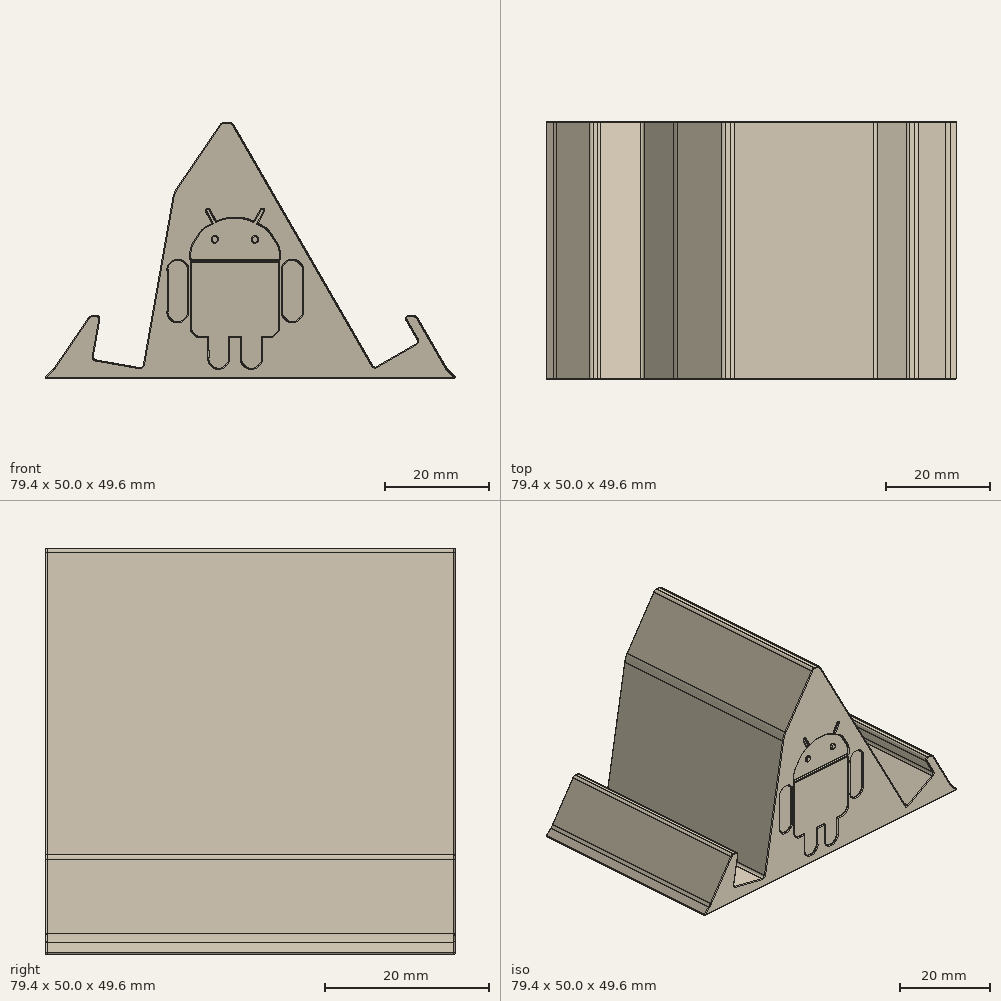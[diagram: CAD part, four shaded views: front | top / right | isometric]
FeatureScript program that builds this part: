
annotation { "Feature Type Name" : "Feature", "Feature Type Description" : "" }
export const myFeature = defineFeature(function(context is Context, id is Id, definition is map)
    precondition{}
    {
        {
            var Q0;
            Q0=qCreatedBy(makeId("Front.planeOp"),FACE);
            var sketch = newSketch(context, id + "F0", { "sketchPlane" : qUnion([Q0])});
            skLineSegment(sketch, "E0", {"start": v(-5.77, 0) * mm, "end": v(5.77, 0) * mm});
            skLineSegment(sketch, "E1", {"start": v(5.77, 0) * mm, "end": v(-0.11, 10.2) * mm});
            skLineSegment(sketch, "E2", {"start": v(0, 0) * mm, "end": v(0, -5.44) * mm, "construction": true});
            skLineSegment(sketch, "E3", {"start": v(-5.77, 0) * mm, "end": v(-33.27, 47.63) * mm});
            skLineSegment(sketch, "E4", {"start": v(-69.73, -2) * mm, "end": v(10.27, -2) * mm});
            skLineSegment(sketch, "E5", {"start": v(5.77, 0) * mm, "end": v(8.27, 0) * mm, "construction": true});
            skLineSegment(sketch, "E6", {"start": v(8.27, 0) * mm, "end": v(10.27, -2) * mm});
            skLineSegment(sketch, "E7", {"start": v(-5.77, 0) * mm, "end": v(-7.77, 0) * mm, "construction": true});
            skLineSegment(sketch, "E8", {"start": v(-69.73, -2) * mm, "end": v(-67.73, 0) * mm});
            skLineSegment(sketch, "E9", {"start": v(-7.77, 0) * mm, "end": v(-35.27, 47.63) * mm});
            skLineSegment(sketch, "E10", {"start": v(-35.27, 47.63) * mm, "end": v(-33.27, 47.63) * mm});
            skLineSegment(sketch, "E11", {"start": v(8.27, 0) * mm, "end": v(2.39, 10.2) * mm});
            skLineSegment(sketch, "E12", {"start": v(2.39, 10.2) * mm, "end": v(-0.11, 10.2) * mm});
            skLineSegment(sketch, "E13", {"start": v(-7.77, 0) * mm, "end": v(-67.73, 0) * mm});
            skLineSegment(sketch, "E14", {"start": v(8.27, 0) * mm, "end": v(8.27, 0) * mm});
            skLineSegment(sketch, "E15", {"start": v(-5.77, 0) * mm, "end": v(2.89, 5) * mm});
            skSolve(sketch);
        }
        {
            var Q0;
            Q0=makeQuery(id+"F0.imprint","IMPRINT",FACE,{"disambiguationData":[TD([[makeQuery(id+"F0.imprint","IMPRINT",EDGE,{"derivedFrom":sQuery(id+"F0.wireOp",EDGE,"E0")}),-1.0]])]});
            var Q1;
            {var subQ0=sQuery(id+"F0.wireOp",EDGE,"E0");Q1=makeQuery(id+"F0.imprint","IMPRINT",FACE,{"disambiguationData":[TD([[makeQuery(id+"F0.imprint","IMPRINT",EDGE,{"derivedFrom":subQ0}),1.0]])]});}
            extrude(context, id + "F1", {"entities" : qUnion([Q0, Q1]), "depth" : 50 * mm});
        }
        {
            var Q0;
            Q0=qCreatedBy(makeId("Top.planeOp"),FACE);
            var sketch = newSketch(context, id + "F2", { "sketchPlane" : qUnion([Q0])});
            skPoint(sketch, "E16.0", {"position": v(-69.73, -25) * mm});
            skPoint(sketch, "E16.1", {"position": v(-35.27, -25) * mm});
            skLineSegment(sketch, "E17.bottom", {"start": v(-69.73, -3) * mm, "end": v(-7.77, -3) * mm});
            skLineSegment(sketch, "E17.top", {"start": v(-69.73, -47) * mm, "end": v(-7.77, -47) * mm});
            skLineSegment(sketch, "E17.left", {"start": v(-69.73, -3) * mm, "end": v(-69.73, -47) * mm});
            skLineSegment(sketch, "E17.right", {"start": v(-7.77, -3) * mm, "end": v(-7.77, -47) * mm});
            skPoint(sketch, "E18.1", {"position": v(-7.77, -25) * mm});
            skPoint(sketch, "E19.0", {"position": v(-69.73, 0) * mm});
            skSolve(sketch);
        }
        {
            var Q0;
            Q0=makeQuery(id+"F2.imprint","IMPRINT",FACE,{"disambiguationData":[TD([[makeQuery(id+"F2.imprint","IMPRINT",EDGE,{"derivedFrom":sQuery(id+"F2.wireOp",EDGE,"E17.bottom")}),-1.0]])]});
            extrude(context, id + "F3", {"entities" : qUnion([Q0]), "operationType" : NewBodyOperationType.REMOVE, "endBound" : BoundingType.THROUGH_ALL, "oppositeDirection" : true, "depth" : 25 * mm});
        }
        {
            var Q0;
            Q0=makeQuery(id+"F1.opExtrude","CAP_FACE",FACE,{"disambiguationData":[OSD([sQuery(id+"F0.wireOp",EDGE,"E1"),sQuery(id+"F0.wireOp",EDGE,"E3"),sQuery(id+"F0.wireOp",EDGE,"E4"),sQuery(id+"F0.wireOp",EDGE,"E6"),sQuery(id+"F0.wireOp",EDGE,"E8"),sQuery(id+"F0.wireOp",EDGE,"E9"),sQuery(id+"F0.wireOp",EDGE,"E10"),sQuery(id+"F0.wireOp",EDGE,"E11"),sQuery(id+"F0.wireOp",EDGE,"E12"),sQuery(id+"F0.wireOp",EDGE,"E13"),sQuery(id+"F0.wireOp",EDGE,"E14"),sQuery(id+"F0.wireOp",EDGE,"E15")])],"isStart":false});
            var sketch = newSketch(context, id + "F4", { "sketchPlane" : qUnion([Q0])});
            skPoint(sketch, "E20.0", {"position": v(-67.73, 0) * mm});
            skPoint(sketch, "E21.0", {"position": v(-35.27, 47.63) * mm});
            skLineSegment(sketch, "E22", {"start": v(-67.73, 0) * mm, "end": v(-35.27, 47.63) * mm});
            skLineSegment(sketch, "E23", {"start": v(-65.55, 0) * mm, "end": v(-34.27, 45.9) * mm});
            skLineSegment(sketch, "E24", {"start": v(-35.27, 47.63) * mm, "end": v(-34.27, 45.9) * mm});
            skLineSegment(sketch, "E25", {"start": v(-67.73, 0) * mm, "end": v(-65.55, 0) * mm});
            skSolve(sketch);
        }
        {
            var Q0;
            Q0=makeQuery(id+"F4.imprint","IMPRINT",FACE,{"disambiguationData":[TD([[makeQuery(id+"F4.imprint","IMPRINT",EDGE,{"derivedFrom":sQuery(id+"F4.wireOp",EDGE,"E22")}),-1.0]])]});
            var Q1;
            Q1=makeQuery(id+"F3.boolean.opBoolean","COPY",FACE,{"derivedFrom":makeQuery(id+"F3.opExtrude","SWEPT_FACE",FACE,{"disambiguationData":[OSD([sQuery(id+"F2.wireOp",EDGE,"E17.top")])]})});
            extrude(context, id + "F5", {"entities" : qUnion([Q0]), "operationType" : NewBodyOperationType.ADD, "endBound" : BoundingType.UP_TO_SURFACE, "oppositeDirection" : true, "endBoundEntityFace" : qUnion([Q1]), "depth" : 25 * mm});
        }
        {
            var Q0;
            Q0=makeQuery(id+"F1.opExtrude","CAP_FACE",FACE,{"disambiguationData":[OSD([sQuery(id+"F0.wireOp",EDGE,"E1"),sQuery(id+"F0.wireOp",EDGE,"E3"),sQuery(id+"F0.wireOp",EDGE,"E4"),sQuery(id+"F0.wireOp",EDGE,"E6"),sQuery(id+"F0.wireOp",EDGE,"E8"),sQuery(id+"F0.wireOp",EDGE,"E9"),sQuery(id+"F0.wireOp",EDGE,"E10"),sQuery(id+"F0.wireOp",EDGE,"E11"),sQuery(id+"F0.wireOp",EDGE,"E12"),sQuery(id+"F0.wireOp",EDGE,"E13"),sQuery(id+"F0.wireOp",EDGE,"E14"),sQuery(id+"F0.wireOp",EDGE,"E15")])],"isStart":true});
            var sketch = newSketch(context, id + "F6", { "sketchPlane" : qUnion([Q0])});
            skPoint(sketch, "E26.0", {"position": v(35.27, 47.63) * mm});
            skPoint(sketch, "E26.1", {"position": v(67.73, 0) * mm});
            skLineSegment(sketch, "E27", {"start": v(67.73, 0) * mm, "end": v(35.27, 47.63) * mm});
            skLineSegment(sketch, "E28", {"start": v(65.55, 0) * mm, "end": v(34.27, 45.9) * mm});
            skLineSegment(sketch, "E29", {"start": v(34.27, 45.9) * mm, "end": v(35.27, 47.63) * mm});
            skLineSegment(sketch, "E30", {"start": v(65.55, 0) * mm, "end": v(67.73, 0) * mm});
            skSolve(sketch);
        }
        {
            var Q0;
            Q0=makeQuery(id+"F6.imprint","IMPRINT",FACE,{"disambiguationData":[TD([[makeQuery(id+"F6.imprint","IMPRINT",EDGE,{"derivedFrom":sQuery(id+"F6.wireOp",EDGE,"E27")}),1.0]])]});
            var Q1;
            Q1=makeQuery(id+"F3.boolean.opBoolean","COPY",FACE,{"derivedFrom":makeQuery(id+"F3.opExtrude","SWEPT_FACE",FACE,{"disambiguationData":[OSD([sQuery(id+"F2.wireOp",EDGE,"E17.bottom")])]})});
            extrude(context, id + "F7", {"entities" : qUnion([Q0]), "operationType" : NewBodyOperationType.ADD, "endBound" : BoundingType.UP_TO_SURFACE, "oppositeDirection" : true, "endBoundEntityFace" : qUnion([Q1]), "depth" : 25 * mm});
        }
        {
            var Q0;
            {var subQ2=sQuery(id+"F0.wireOp",EDGE,"E13");Q0=makeQuery(id+"F3.boolean.opBoolean","SPLIT",FACE,{"disambiguationData":[TD([makeQuery(id+"F3.opExtrude","SWEPT_FACE",FACE,{"disambiguationData":[OSD([sQuery(id+"F2.wireOp",EDGE,"E17.top")])]})])],"derivedFrom":makeQuery(id+"F1.opExtrude","SWEPT_FACE",FACE,{"disambiguationData":[OSD([subQ2])]})});}
            var Q1;
            {var subQ2=sQuery(id+"F0.wireOp",EDGE,"E13");Q1=makeQuery(id+"F3.boolean.opBoolean","SPLIT",FACE,{"disambiguationData":[TD([makeQuery(id+"F3.opExtrude","SWEPT_FACE",FACE,{"disambiguationData":[OSD([sQuery(id+"F2.wireOp",EDGE,"E17.bottom")])]})])],"derivedFrom":makeQuery(id+"F1.opExtrude","SWEPT_FACE",FACE,{"disambiguationData":[OSD([subQ2])]})});}
            var Q2;
            Q2=makeQuery(id+"F1.opExtrude","SWEPT_BODY",BODY,{"disambiguationData":[OSD([sQuery(id+"F0.wireOp",EDGE,"E1"),sQuery(id+"F0.wireOp",EDGE,"E3"),sQuery(id+"F0.wireOp",EDGE,"E4"),sQuery(id+"F0.wireOp",EDGE,"E6"),sQuery(id+"F0.wireOp",EDGE,"E8"),sQuery(id+"F0.wireOp",EDGE,"E9"),sQuery(id+"F0.wireOp",EDGE,"E10"),sQuery(id+"F0.wireOp",EDGE,"E11"),sQuery(id+"F0.wireOp",EDGE,"E12"),sQuery(id+"F0.wireOp",EDGE,"E13"),sQuery(id+"F0.wireOp",EDGE,"E14"),sQuery(id+"F0.wireOp",EDGE,"E15")])]});
            extrude(context, id + "F8", {"entities" : qUnion([Q0, Q1]), "operationType" : NewBodyOperationType.ADD, "endBound" : BoundingType.UP_TO_BODY, "endBoundEntityBody" : qUnion([Q2]), "depth" : 25 * mm});
        }
        {
            var Q0;
            {var subQ0=sQuery(id+"F0.wireOp",EDGE,"E13");Q0=makeQuery(id+"F8.boolean.opBoolean","MERGE",FACE,{"derivedFrom":[makeQuery(id+"F5.boolean.opBoolean","MERGE",FACE,{"derivedFrom":[makeQuery(id+"F1.opExtrude","CAP_FACE",FACE,{"disambiguationData":[OSD([sQuery(id+"F0.wireOp",EDGE,"E1"),sQuery(id+"F0.wireOp",EDGE,"E3"),sQuery(id+"F0.wireOp",EDGE,"E4"),sQuery(id+"F0.wireOp",EDGE,"E6"),sQuery(id+"F0.wireOp",EDGE,"E8"),sQuery(id+"F0.wireOp",EDGE,"E9"),sQuery(id+"F0.wireOp",EDGE,"E10"),sQuery(id+"F0.wireOp",EDGE,"E11"),sQuery(id+"F0.wireOp",EDGE,"E12"),subQ0,sQuery(id+"F0.wireOp",EDGE,"E15")])],"isStart":false}),makeQuery(id+"F5.opExtrude","CAP_FACE",FACE,{"disambiguationData":[OSD([sQuery(id+"F4.wireOp",EDGE,"E22"),sQuery(id+"F4.wireOp",EDGE,"E23"),sQuery(id+"F4.wireOp",EDGE,"E24"),sQuery(id+"F4.wireOp",EDGE,"E25")])],"isStart":true})]}),makeQuery(id+"F8.opExtrude","SWEPT_FACE",FACE,{"disambiguationData":[OSD([subQ0]),TDD([makeQuery(id+"F1.opExtrude","CAP_EDGE",EDGE,{"disambiguationData":[OSD([subQ0])],"isStart":false})])]})]});}
            var sketch = newSketch(context, id + "F9", { "sketchPlane" : qUnion([Q0])});
            skLineSegment(sketch, "E31", {"start": v(-71.82, 0) * mm, "end": v(0, 0) * mm, "construction": true});
            skLineSegment(sketch, "E32", {"start": v(-60.58, 0) * mm, "end": v(-60.28, 1.71) * mm, "construction": true});
            skLineSegment(sketch, "E33", {"start": v(-53.78, 38.57) * mm, "end": v(-43.78, 38.57) * mm});
            skLineSegment(sketch, "E34", {"start": v(-43.78, 38.57) * mm, "end": v(-50.58, 0) * mm});
            skLineSegment(sketch, "E35", {"start": v(-50.58, 0) * mm, "end": v(-60.58, 0) * mm, "construction": true});
            skLineSegment(sketch, "E36", {"start": v(-50.58, 0) * mm, "end": v(-60.28, 1.71) * mm});
            skLineSegment(sketch, "E37", {"start": v(-60.28, 1.71) * mm, "end": v(-53.78, 38.57) * mm});
            skLineSegment(sketch, "E38", {"start": v(-58.78, 10.2) * mm, "end": v(-60.78, 10.2) * mm});
            skLineSegment(sketch, "E39", {"start": v(-50.58, 0) * mm, "end": v(-50.58, -2) * mm});
            skPoint(sketch, "E40.0", {"position": v(-35.27, 47.63) * mm});
            skLineSegment(sketch, "E41", {"start": v(-35.27, 47.63) * mm, "end": v(-33.62, 46.5) * mm});
            skLineSegment(sketch, "E42", {"start": v(-33.62, 46.5) * mm, "end": v(-42.74, 33.13) * mm});
            skLineSegment(sketch, "E43", {"start": v(-42.74, 33.13) * mm, "end": v(-48.58, 0) * mm});
            skLineSegment(sketch, "E44", {"start": v(-48.58, 0) * mm, "end": v(-48.58, -2) * mm});
            skLineSegment(sketch, "E45", {"start": v(-48.58, -2) * mm, "end": v(-50.58, -2) * mm});
            skLineSegment(sketch, "E46", {"start": v(-42.74, 33.13) * mm, "end": v(-44.74, 33.13) * mm, "construction": true});
            skSolve(sketch);
        }
        {
            var Q0;
            {var subQ0=sQuery(id+"F9.wireOp",EDGE,"E33");Q0=makeQuery(id+"F9.imprint","IMPRINT",FACE,{"disambiguationData":[TD([[makeQuery(id+"F9.imprint","IMPRINT",EDGE,{"derivedFrom":subQ0}),-1.0]])]});}
            var Q1;
            {var subQ4=sQuery(id+"F9.wireOp",EDGE,"E36");Q1=makeQuery(id+"F9.imprint","IMPRINT",FACE,{"disambiguationData":[TD([[makeQuery(id+"F9.imprint","IMPRINT",EDGE,{"derivedFrom":subQ4}),-1.0]])]});}
            var Q2;
            {var subQ0=sQuery(id+"F9.wireOp",EDGE,"E38");Q2=makeQuery(id+"F9.imprint","IMPRINT",FACE,{"disambiguationData":[TD([[makeQuery(id+"F9.imprint","IMPRINT",EDGE,{"derivedFrom":subQ0}),-1.0]])]});}
            extrude(context, id + "F10", {"entities" : qUnion([Q0, Q1, Q2]), "operationType" : NewBodyOperationType.REMOVE, "endBound" : BoundingType.THROUGH_ALL, "oppositeDirection" : true, "depth" : 25 * mm});
        }
        {
            var Q0;
            {var subQ2=sQuery(id+"F9.wireOp",EDGE,"E36");Q0=makeQuery(id+"F9.imprint","IMPRINT",FACE,{"disambiguationData":[TD([[makeQuery(id+"F9.imprint","IMPRINT",EDGE,{"derivedFrom":subQ2}),1.0]])]});}
            var Q1;
            {var subQ0=sQuery(id+"F2.wireOp",EDGE,"E17.bottom");Q1=makeQuery(id+"F8.boolean.opBoolean","MERGE",FACE,{"derivedFrom":[makeQuery(id+"F7.boolean.opBoolean","MERGE",FACE,{"derivedFrom":[makeQuery(id+"F3.boolean.opBoolean","COPY",FACE,{"derivedFrom":makeQuery(id+"F3.opExtrude","SWEPT_FACE",FACE,{"disambiguationData":[OSD([subQ0])]})}),makeQuery(id+"F7.opExtrude","CAP_FACE",FACE,{"disambiguationData":[OSD([sQuery(id+"F6.wireOp",EDGE,"E27"),sQuery(id+"F6.wireOp",EDGE,"E28"),sQuery(id+"F6.wireOp",EDGE,"E29"),sQuery(id+"F6.wireOp",EDGE,"E30")])],"isStart":false})]}),makeQuery(id+"F8.opExtrude","SWEPT_FACE",FACE,{"disambiguationData":[OSD([subQ0])]})]});}
            extrude(context, id + "F11", {"entities" : qUnion([Q0]), "operationType" : NewBodyOperationType.ADD, "endBound" : BoundingType.UP_TO_SURFACE, "oppositeDirection" : true, "endBoundEntityFace" : qUnion([Q1]), "depth" : 25 * mm});
        }
        {
            var Q0;
            {var subQ1=sQuery(id+"F9.wireOp",EDGE,"E39");Q0=makeQuery(id+"F9.imprint","IMPRINT",FACE,{"disambiguationData":[TD([[makeQuery(id+"F9.imprint","IMPRINT",EDGE,{"derivedFrom":subQ1}),1.0]])]});}
            var Q1;
            {var subQ0=sQuery(id+"F2.wireOp",EDGE,"E17.bottom");Q1=makeQuery(id+"F8.boolean.opBoolean","MERGE",FACE,{"derivedFrom":[makeQuery(id+"F7.boolean.opBoolean","MERGE",FACE,{"derivedFrom":[makeQuery(id+"F3.boolean.opBoolean","COPY",FACE,{"derivedFrom":makeQuery(id+"F3.opExtrude","SWEPT_FACE",FACE,{"disambiguationData":[OSD([subQ0])]})}),makeQuery(id+"F7.opExtrude","CAP_FACE",FACE,{"disambiguationData":[OSD([sQuery(id+"F6.wireOp",EDGE,"E27"),sQuery(id+"F6.wireOp",EDGE,"E28"),sQuery(id+"F6.wireOp",EDGE,"E29"),sQuery(id+"F6.wireOp",EDGE,"E30")])],"isStart":false})]}),makeQuery(id+"F8.opExtrude","SWEPT_FACE",FACE,{"disambiguationData":[OSD([subQ0])]})]});}
            extrude(context, id + "F12", {"entities" : qUnion([Q0]), "operationType" : NewBodyOperationType.ADD, "endBound" : BoundingType.UP_TO_SURFACE, "oppositeDirection" : true, "endBoundEntityFace" : qUnion([Q1]), "depth" : 25 * mm});
        }
        {
            var Q0;
            {var subQ0=sQuery(id+"F0.wireOp",EDGE,"E13");Q0=makeQuery(id+"F8.boolean.opBoolean","MERGE",FACE,{"derivedFrom":[makeQuery(id+"F5.boolean.opBoolean","MERGE",FACE,{"derivedFrom":[makeQuery(id+"F1.opExtrude","CAP_FACE",FACE,{"disambiguationData":[OSD([sQuery(id+"F0.wireOp",EDGE,"E1"),sQuery(id+"F0.wireOp",EDGE,"E3"),sQuery(id+"F0.wireOp",EDGE,"E4"),sQuery(id+"F0.wireOp",EDGE,"E6"),sQuery(id+"F0.wireOp",EDGE,"E8"),sQuery(id+"F0.wireOp",EDGE,"E9"),sQuery(id+"F0.wireOp",EDGE,"E10"),sQuery(id+"F0.wireOp",EDGE,"E11"),sQuery(id+"F0.wireOp",EDGE,"E12"),subQ0,sQuery(id+"F0.wireOp",EDGE,"E15")])],"isStart":false}),makeQuery(id+"F5.opExtrude","CAP_FACE",FACE,{"disambiguationData":[OSD([sQuery(id+"F4.wireOp",EDGE,"E22"),sQuery(id+"F4.wireOp",EDGE,"E23"),sQuery(id+"F4.wireOp",EDGE,"E24"),sQuery(id+"F4.wireOp",EDGE,"E25")])],"isStart":true})]}),makeQuery(id+"F8.opExtrude","SWEPT_FACE",FACE,{"disambiguationData":[OSD([subQ0]),TDD([makeQuery(id+"F1.opExtrude","CAP_EDGE",EDGE,{"disambiguationData":[OSD([subQ0])],"isStart":false})])]})]});}
            var sketch = newSketch(context, id + "F13", { "sketchPlane" : qUnion([Q0])});
            skFitSpline(sketch, "E47", {"points": [v(-43.8, 20.82) * mm, v(-44.33, 20.82) * mm, v(-44.78, 20.64) * mm, v(-45.15, 20.27) * mm]});
            skFitSpline(sketch, "E48", {"points": [v(-45.15, 20.27) * mm, v(-45.52, 19.9) * mm, v(-45.7, 19.45) * mm, v(-45.7, 18.94) * mm]});
            skLineSegment(sketch, "E49", {"start": v(-45.7, 18.94) * mm, "end": v(-45.7, 11) * mm});
            skFitSpline(sketch, "E50", {"points": [v(-45.7, 11) * mm, v(-45.7, 10.47) * mm, v(-45.52, 10.02) * mm, v(-45.15, 9.65) * mm]});
            skFitSpline(sketch, "E51", {"points": [v(-45.15, 9.65) * mm, v(-44.78, 9.28) * mm, v(-44.33, 9.1) * mm, v(-43.8, 9.1) * mm]});
            skFitSpline(sketch, "E52", {"points": [v(-43.8, 9.1) * mm, v(-43.27, 9.1) * mm, v(-42.82, 9.28) * mm, v(-42.46, 9.65) * mm]});
            skFitSpline(sketch, "E53", {"points": [v(-42.46, 9.65) * mm, v(-42.1, 10.02) * mm, v(-41.91, 10.47) * mm, v(-41.91, 11) * mm]});
            skLineSegment(sketch, "E54", {"start": v(-41.91, 11) * mm, "end": v(-41.91, 18.94) * mm});
            skFitSpline(sketch, "E55", {"points": [v(-41.91, 18.94) * mm, v(-41.91, 19.45) * mm, v(-42.1, 19.9) * mm, v(-42.47, 20.27) * mm]});
            skFitSpline(sketch, "E56", {"points": [v(-42.47, 20.27) * mm, v(-42.84, 20.64) * mm, v(-43.28, 20.82) * mm, v(-43.8, 20.82) * mm]});
            skLineSegment(sketch, "E57", {"start": v(-28.5, 27.95) * mm, "end": v(-27.2, 30.37) * mm});
            skFitSpline(sketch, "E58", {"points": [v(-27.2, 30.37) * mm, v(-27.11, 30.53) * mm, v(-27.14, 30.65) * mm, v(-27.29, 30.74) * mm]});
            skFitSpline(sketch, "E59", {"points": [v(-27.29, 30.74) * mm, v(-27.45, 30.81) * mm, v(-27.57, 30.77) * mm, v(-27.66, 30.63) * mm]});
            skLineSegment(sketch, "E60", {"start": v(-27.66, 30.63) * mm, "end": v(-28.99, 28.19) * mm});
            skFitSpline(sketch, "E61", {"points": [v(-28.99, 28.19) * mm, v(-30.16, 28.7) * mm, v(-31.4, 28.96) * mm, v(-32.7, 28.96) * mm]});
            skFitSpline(sketch, "E62", {"points": [v(-32.7, 28.96) * mm, v(-34, 28.96) * mm, v(-35.24, 28.7) * mm, v(-36.41, 28.19) * mm]});
            skLineSegment(sketch, "E63", {"start": v(-36.41, 28.19) * mm, "end": v(-37.74, 30.63) * mm});
            skFitSpline(sketch, "E64", {"points": [v(-37.74, 30.63) * mm, v(-37.83, 30.77) * mm, v(-37.95, 30.81) * mm, v(-38.11, 30.74) * mm]});
            skFitSpline(sketch, "E65", {"points": [v(-38.11, 30.74) * mm, v(-38.26, 30.65) * mm, v(-38.29, 30.53) * mm, v(-38.2, 30.37) * mm]});
            skLineSegment(sketch, "E66", {"start": v(-38.2, 30.37) * mm, "end": v(-36.9, 27.95) * mm});
            skFitSpline(sketch, "E67", {"points": [v(-36.9, 27.95) * mm, v(-38.22, 27.27) * mm, v(-39.28, 26.33) * mm, v(-40.07, 25.11) * mm]});
            skFitSpline(sketch, "E68", {"points": [v(-40.07, 25.11) * mm, v(-40.86, 23.9) * mm, v(-41.25, 22.57) * mm, v(-41.25, 21.13) * mm]});
            skLineSegment(sketch, "E69", {"start": v(-41.25, 21.13) * mm, "end": v(-24.17, 21.13) * mm});
            skFitSpline(sketch, "E70", {"points": [v(-24.17, 21.13) * mm, v(-24.17, 22.57) * mm, v(-24.56, 23.9) * mm, v(-25.35, 25.11) * mm]});
            skFitSpline(sketch, "E71", {"points": [v(-25.35, 25.11) * mm, v(-26.14, 26.33) * mm, v(-27.2, 27.27) * mm, v(-28.5, 27.95) * mm]});
            skFitSpline(sketch, "E72", {"points": [v(-36.09, 24.43) * mm, v(-36.23, 24.29) * mm, v(-36.4, 24.22) * mm, v(-36.6, 24.22) * mm]});
            skFitSpline(sketch, "E73", {"points": [v(-36.6, 24.22) * mm, v(-36.8, 24.22) * mm, v(-36.96, 24.29) * mm, v(-37.1, 24.43) * mm]});
            skFitSpline(sketch, "E74", {"points": [v(-37.1, 24.43) * mm, v(-37.23, 24.57) * mm, v(-37.3, 24.74) * mm, v(-37.3, 24.94) * mm]});
            skFitSpline(sketch, "E75", {"points": [v(-37.3, 24.94) * mm, v(-37.3, 25.14) * mm, v(-37.23, 25.3) * mm, v(-37.1, 25.45) * mm]});
            skFitSpline(sketch, "E76", {"points": [v(-37.1, 25.45) * mm, v(-36.96, 25.59) * mm, v(-36.8, 25.66) * mm, v(-36.6, 25.66) * mm]});
            skFitSpline(sketch, "E77", {"points": [v(-36.6, 25.66) * mm, v(-36.4, 25.66) * mm, v(-36.23, 25.59) * mm, v(-36.09, 25.45) * mm]});
            skFitSpline(sketch, "E78", {"points": [v(-36.09, 25.45) * mm, v(-35.95, 25.3) * mm, v(-35.88, 25.14) * mm, v(-35.88, 24.94) * mm]});
            skFitSpline(sketch, "E79", {"points": [v(-35.88, 24.94) * mm, v(-35.88, 24.74) * mm, v(-35.95, 24.57) * mm, v(-36.09, 24.43) * mm]});
            skFitSpline(sketch, "E80", {"points": [v(-28.3, 24.43) * mm, v(-28.44, 24.29) * mm, v(-28.6, 24.22) * mm, v(-28.8, 24.22) * mm]});
            skFitSpline(sketch, "E81", {"points": [v(-28.8, 24.22) * mm, v(-29, 24.22) * mm, v(-29.17, 24.29) * mm, v(-29.31, 24.43) * mm]});
            skFitSpline(sketch, "E82", {"points": [v(-29.31, 24.43) * mm, v(-29.45, 24.57) * mm, v(-29.52, 24.74) * mm, v(-29.52, 24.94) * mm]});
            skFitSpline(sketch, "E83", {"points": [v(-29.52, 24.94) * mm, v(-29.52, 25.14) * mm, v(-29.45, 25.3) * mm, v(-29.31, 25.45) * mm]});
            skFitSpline(sketch, "E84", {"points": [v(-29.31, 25.45) * mm, v(-29.17, 25.59) * mm, v(-29, 25.66) * mm, v(-28.8, 25.66) * mm]});
            skFitSpline(sketch, "E85", {"points": [v(-28.8, 25.66) * mm, v(-28.6, 25.66) * mm, v(-28.44, 25.59) * mm, v(-28.3, 25.45) * mm]});
            skFitSpline(sketch, "E86", {"points": [v(-28.3, 25.45) * mm, v(-28.17, 25.3) * mm, v(-28.1, 25.14) * mm, v(-28.1, 24.94) * mm]});
            skFitSpline(sketch, "E87", {"points": [v(-28.1, 24.94) * mm, v(-28.1, 24.74) * mm, v(-28.17, 24.57) * mm, v(-28.3, 24.43) * mm]});
            skFitSpline(sketch, "E88", {"points": [v(-41.18, 8.17) * mm, v(-41.18, 7.6) * mm, v(-40.98, 7.12) * mm, v(-40.59, 6.73) * mm]});
            skFitSpline(sketch, "E89", {"points": [v(-40.59, 6.73) * mm, v(-40.2, 6.34) * mm, v(-39.71, 6.14) * mm, v(-39.14, 6.14) * mm]});
            skLineSegment(sketch, "E90", {"start": v(-39.14, 6.14) * mm, "end": v(-37.78, 6.14) * mm});
            skLineSegment(sketch, "E91", {"start": v(-37.78, 6.14) * mm, "end": v(-37.76, 1.95) * mm});
            skFitSpline(sketch, "E92", {"points": [v(-37.76, 1.95) * mm, v(-37.76, 1.42) * mm, v(-37.58, 0.97) * mm, v(-37.2, 0.6) * mm]});
            skFitSpline(sketch, "E93", {"points": [v(-37.2, 0.6) * mm, v(-36.84, 0.23) * mm, v(-36.4, 0.05) * mm, v(-35.88, 0.05) * mm]});
            skFitSpline(sketch, "E94", {"points": [v(-35.88, 0.05) * mm, v(-35.35, 0.05) * mm, v(-34.9, 0.23) * mm, v(-34.53, 0.6) * mm]});
            skFitSpline(sketch, "E95", {"points": [v(-34.53, 0.6) * mm, v(-34.16, 0.97) * mm, v(-33.97, 1.42) * mm, v(-33.97, 1.95) * mm]});
            skLineSegment(sketch, "E96", {"start": v(-33.97, 1.95) * mm, "end": v(-33.97, 6.14) * mm});
            skLineSegment(sketch, "E97", {"start": v(-33.97, 6.14) * mm, "end": v(-31.43, 6.14) * mm});
            skLineSegment(sketch, "E98", {"start": v(-31.43, 6.14) * mm, "end": v(-31.43, 1.95) * mm});
            skFitSpline(sketch, "E99", {"points": [v(-31.43, 1.95) * mm, v(-31.43, 1.42) * mm, v(-31.24, 0.97) * mm, v(-30.87, 0.6) * mm]});
            skFitSpline(sketch, "E100", {"points": [v(-30.87, 0.6) * mm, v(-30.5, 0.23) * mm, v(-30.05, 0.05) * mm, v(-29.52, 0.05) * mm]});
            skFitSpline(sketch, "E101", {"points": [v(-29.52, 0.05) * mm, v(-29, 0.05) * mm, v(-28.55, 0.23) * mm, v(-28.18, 0.6) * mm]});
            skFitSpline(sketch, "E102", {"points": [v(-28.18, 0.6) * mm, v(-27.8, 0.97) * mm, v(-27.62, 1.42) * mm, v(-27.62, 1.95) * mm]});
            skLineSegment(sketch, "E103", {"start": v(-27.62, 1.95) * mm, "end": v(-27.62, 6.14) * mm});
            skLineSegment(sketch, "E104", {"start": v(-27.62, 6.14) * mm, "end": v(-26.24, 6.14) * mm});
            skFitSpline(sketch, "E105", {"points": [v(-26.24, 6.14) * mm, v(-25.68, 6.14) * mm, v(-25.21, 6.34) * mm, v(-24.82, 6.73) * mm]});
            skFitSpline(sketch, "E106", {"points": [v(-24.82, 6.73) * mm, v(-24.42, 7.12) * mm, v(-24.23, 7.6) * mm, v(-24.23, 8.17) * mm]});
            skLineSegment(sketch, "E107", {"start": v(-24.23, 8.17) * mm, "end": v(-24.23, 20.47) * mm});
            skLineSegment(sketch, "E108", {"start": v(-24.23, 20.47) * mm, "end": v(-41.18, 20.47) * mm});
            skLineSegment(sketch, "E109", {"start": v(-41.18, 20.47) * mm, "end": v(-41.18, 8.17) * mm});
            skFitSpline(sketch, "E110", {"points": [v(-21.6, 20.82) * mm, v(-22.12, 20.82) * mm, v(-22.56, 20.64) * mm, v(-22.93, 20.28) * mm]});
            skFitSpline(sketch, "E111", {"points": [v(-22.93, 20.28) * mm, v(-23.3, 19.91) * mm, v(-23.49, 19.47) * mm, v(-23.49, 18.94) * mm]});
            skLineSegment(sketch, "E112", {"start": v(-23.49, 18.94) * mm, "end": v(-23.49, 11) * mm});
            skFitSpline(sketch, "E113", {"points": [v(-23.49, 11) * mm, v(-23.49, 10.47) * mm, v(-23.3, 10.02) * mm, v(-22.93, 9.65) * mm]});
            skFitSpline(sketch, "E114", {"points": [v(-22.93, 9.65) * mm, v(-22.56, 9.28) * mm, v(-22.12, 9.1) * mm, v(-21.6, 9.1) * mm]});
            skFitSpline(sketch, "E115", {"points": [v(-21.6, 9.1) * mm, v(-21.07, 9.1) * mm, v(-20.62, 9.28) * mm, v(-20.25, 9.65) * mm]});
            skFitSpline(sketch, "E116", {"points": [v(-20.25, 9.65) * mm, v(-19.88, 10.02) * mm, v(-19.7, 10.47) * mm, v(-19.7, 11) * mm]});
            skLineSegment(sketch, "E117", {"start": v(-19.7, 11) * mm, "end": v(-19.7, 18.94) * mm});
            skFitSpline(sketch, "E118", {"points": [v(-19.7, 18.94) * mm, v(-19.7, 19.47) * mm, v(-19.88, 19.91) * mm, v(-20.25, 20.28) * mm]});
            skFitSpline(sketch, "E119", {"points": [v(-20.25, 20.28) * mm, v(-20.62, 20.64) * mm, v(-21.07, 20.82) * mm, v(-21.6, 20.82) * mm]});
            skSolve(sketch);
        }
        {
            var Q0;
            Q0=makeQuery(id+"F13.imprint","IMPRINT",FACE,{"disambiguationData":[TD([[makeQuery(id+"F13.imprint","IMPRINT",EDGE,{"derivedFrom":sQuery(id+"F13.wireOp",EDGE,"E57")}),1.0]])]});
            var Q1;
            Q1=makeQuery(id+"F13.imprint","IMPRINT",FACE,{"disambiguationData":[TD([[makeQuery(id+"F13.imprint","IMPRINT",EDGE,{"derivedFrom":sQuery(id+"F13.wireOp",EDGE,"E88")}),1.0]])]});
            var Q2;
            Q2=makeQuery(id+"F13.imprint","IMPRINT",FACE,{"disambiguationData":[TD([[makeQuery(id+"F13.imprint","IMPRINT",EDGE,{"derivedFrom":sQuery(id+"F13.wireOp",EDGE,"E47")}),1.0]])]});
            var Q3;
            Q3=makeQuery(id+"F13.imprint","IMPRINT",FACE,{"disambiguationData":[TD([[makeQuery(id+"F13.imprint","IMPRINT",EDGE,{"derivedFrom":sQuery(id+"F13.wireOp",EDGE,"E110")}),1.0]])]});
            extrude(context, id + "F14", {"entities" : qUnion([Q0, Q1, Q2, Q3]), "operationType" : NewBodyOperationType.REMOVE, "oppositeDirection" : true, "depth" : 0.4 * mm});
        }
        {
            var Q0;
            {var subQ0=sQuery(id+"F9.wireOp",EDGE,"E34");var subQ1=sQuery(id+"F4.wireOp",EDGE,"E22");var subQ2=makeQuery(id+"F10.opExtrude","SWEPT_FACE",FACE,{"disambiguationData":[OSD([subQ0])]});Q0=makeQuery(id+"F12.boolean.opBoolean","MERGE",EDGE,{"derivedFrom":[makeQuery(id+"F10.boolean.opBoolean","INTERSECT",EDGE,{"derivedFrom":[makeQuery(id+"F5.opExtrude","SWEPT_FACE",FACE,{"disambiguationData":[OSD([subQ1])]}),subQ2]}),makeQuery(id+"F10.boolean.opBoolean","INTERSECT",EDGE,{"derivedFrom":[makeQuery(id+"F7.opExtrude","SWEPT_FACE",FACE,{"disambiguationData":[OSD([sQuery(id+"F6.wireOp",EDGE,"E27")])]}),subQ2]}),makeQuery(id+"F12.opExtrude","SWEPT_EDGE",EDGE,{"disambiguationData":[OSD([subQ1,subQ0])]})]});}
            cPlane(context, id + "F15", {"entities" : qUnion([Q0]), "cplaneType" : CPlaneType.MID_PLANE, "offset" : 25 * mm, "width" : 150 * mm, "height" : 150 * mm});
        }
        {
            var Q0;
            Q0=makeQuery(id+"F8.boolean.opBoolean","MERGE",EDGE,{"derivedFrom":[makeQuery(id+"F7.opExtrude","CAP_EDGE",EDGE,{"disambiguationData":[OSD([sQuery(id+"F6.wireOp",EDGE,"E29")])],"isStart":false}),makeQuery(id+"F8.opExtrude","CAP_EDGE",EDGE,{"disambiguationData":[OSD([sQuery(id+"F2.wireOp",EDGE,"E17.bottom")])],"isStart":false})]});
            var Q1;
            {var subQ0=sQuery(id+"F2.wireOp",EDGE,"E17.top");Q1=makeQuery(id+"F8.boolean.opBoolean","MERGE",EDGE,{"derivedFrom":[makeQuery(id+"F5.opExtrude","CAP_EDGE",EDGE,{"disambiguationData":[OSD([sQuery(id+"F4.wireOp",EDGE,"E24")])],"isStart":false}),makeQuery(id+"F8.opExtrude","CAP_EDGE",EDGE,{"disambiguationData":[OSD([subQ0]),topologyDisambiguationEdgeConnected([makeQuery(id+"F1.opExtrude","SWEPT_FACE",FACE,{"disambiguationData":[OSD([sQuery(id+"F0.wireOp",EDGE,"E9")])]})])],"isStart":false})]});}
            var Q2;
            {var subQ0=sQuery(id+"F2.wireOp",EDGE,"E17.top");Q2=makeQuery(id+"F12.boolean.opBoolean","INTERSECT",EDGE,{"derivedFrom":[makeQuery(id+"F8.boolean.opBoolean","MERGE",FACE,{"derivedFrom":[makeQuery(id+"F5.boolean.opBoolean","MERGE",FACE,{"derivedFrom":[makeQuery(id+"F3.boolean.opBoolean","COPY",FACE,{"derivedFrom":makeQuery(id+"F3.opExtrude","SWEPT_FACE",FACE,{"disambiguationData":[OSD([subQ0])]})}),makeQuery(id+"F5.opExtrude","CAP_FACE",FACE,{"disambiguationData":[OSD([sQuery(id+"F4.wireOp",EDGE,"E22"),sQuery(id+"F4.wireOp",EDGE,"E23"),sQuery(id+"F4.wireOp",EDGE,"E24"),sQuery(id+"F4.wireOp",EDGE,"E25")])],"isStart":false})]}),makeQuery(id+"F8.opExtrude","SWEPT_FACE",FACE,{"disambiguationData":[OSD([subQ0])]})]}),makeQuery(id+"F12.opExtrude","SWEPT_FACE",FACE,{"disambiguationData":[OSD([sQuery(id+"F9.wireOp",EDGE,"E43")])]})]});}
            var Q3;
            Q3=makeQuery(id+"F12.opExtrude","CAP_EDGE",EDGE,{"disambiguationData":[OSD([sQuery(id+"F9.wireOp",EDGE,"E43")])],"isStart":false});
            var Q4;
            Q4=makeQuery(id+"F12.opExtrude","CAP_EDGE",EDGE,{"disambiguationData":[OSD([sQuery(id+"F9.wireOp",EDGE,"E42")])],"isStart":false});
            var Q5;
            {var subQ0=sQuery(id+"F2.wireOp",EDGE,"E17.top");Q5=makeQuery(id+"F12.boolean.opBoolean","INTERSECT",EDGE,{"derivedFrom":[makeQuery(id+"F8.boolean.opBoolean","MERGE",FACE,{"derivedFrom":[makeQuery(id+"F5.boolean.opBoolean","MERGE",FACE,{"derivedFrom":[makeQuery(id+"F3.boolean.opBoolean","COPY",FACE,{"derivedFrom":makeQuery(id+"F3.opExtrude","SWEPT_FACE",FACE,{"disambiguationData":[OSD([subQ0])]})}),makeQuery(id+"F5.opExtrude","CAP_FACE",FACE,{"disambiguationData":[OSD([sQuery(id+"F4.wireOp",EDGE,"E22"),sQuery(id+"F4.wireOp",EDGE,"E23"),sQuery(id+"F4.wireOp",EDGE,"E24"),sQuery(id+"F4.wireOp",EDGE,"E25")])],"isStart":false})]}),makeQuery(id+"F8.opExtrude","SWEPT_FACE",FACE,{"disambiguationData":[OSD([subQ0])]})]}),makeQuery(id+"F12.opExtrude","SWEPT_FACE",FACE,{"disambiguationData":[OSD([sQuery(id+"F9.wireOp",EDGE,"E42")])]})]});}
            fillet(context, id + "F16", {"entities" : qUnion([Q0, Q1, Q2, Q3, Q4, Q5]), "radius" : 4 * mm, "tangentPropagation" : true, "allowEdgeOverflow" : false});
        }
        {
            var Q0;
            Q0=makeQuery(id+"F1.opExtrude","SWEPT_EDGE",EDGE,{"disambiguationData":[OSD([sQuery(id+"F0.wireOp",EDGE,"E11"),sQuery(id+"F0.wireOp",EDGE,"E12")])]});
            var Q1;
            Q1=makeQuery(id+"F1.opExtrude","SWEPT_EDGE",EDGE,{"disambiguationData":[OSD([sQuery(id+"F0.wireOp",EDGE,"E3"),sQuery(id+"F0.wireOp",EDGE,"E10")])]});
            var Q2;
            {var subQ0=sQuery(id+"F4.wireOp",EDGE,"E22");var subQ1=sQuery(id+"F0.wireOp",EDGE,"E10");var subQ2=makeQuery(id+"F1.opExtrude","SWEPT_EDGE",EDGE,{"disambiguationData":[OSD([sQuery(id+"F0.wireOp",EDGE,"E9"),subQ1])]});var subQ3=makeQuery(id+"F5.boolean.opBoolean","SPLIT",EDGE,{"derivedFrom":subQ2});Q2=makeQuery(id+"F12.boolean.opBoolean","MERGE",EDGE,{"derivedFrom":[makeQuery(id+"F5.boolean.opBoolean","MERGE",EDGE,{"derivedFrom":[subQ2,makeQuery(id+"F5.opExtrude","SWEPT_EDGE",EDGE,{"disambiguationData":[OSD([subQ1,subQ0,sQuery(id+"F4.wireOp",EDGE,"E24")])]})]}),makeQuery(id+"F7.boolean.opBoolean","MERGE",EDGE,{"derivedFrom":[subQ3,makeQuery(id+"F7.opExtrude","SWEPT_EDGE",EDGE,{"disambiguationData":[OSD([subQ1,sQuery(id+"F6.wireOp",EDGE,"E27"),sQuery(id+"F6.wireOp",EDGE,"E29")])]})]}),makeQuery(id+"F7.boolean.opBoolean","SPLIT",EDGE,{"derivedFrom":subQ3}),makeQuery(id+"F12.opExtrude","SWEPT_EDGE",EDGE,{"disambiguationData":[OSD([subQ1,subQ0,sQuery(id+"F9.wireOp",EDGE,"E41")])]})]});}
            var Q3;
            {var subQ0=sQuery(id+"F9.wireOp",EDGE,"E38");var subQ1=sQuery(id+"F4.wireOp",EDGE,"E22");var subQ3=makeQuery(id+"F10.opExtrude","SWEPT_EDGE",EDGE,{"disambiguationData":[OSD([subQ1,subQ0])]});Q3=makeQuery(id+"F11.boolean.opBoolean","MERGE",EDGE,{"derivedFrom":[makeQuery(id+"F10.boolean.opBoolean","COPY",EDGE,{"disambiguationData":[topologyDisambiguationEdgeConnected([makeQuery(id+"F5.opExtrude","SWEPT_FACE",FACE,{"disambiguationData":[OSD([subQ1])]})])],"derivedFrom":subQ3}),makeQuery(id+"F10.boolean.opBoolean","COPY",EDGE,{"disambiguationData":[topologyDisambiguationEdgeConnected([makeQuery(id+"F7.opExtrude","SWEPT_FACE",FACE,{"disambiguationData":[OSD([sQuery(id+"F6.wireOp",EDGE,"E27")])]})])],"derivedFrom":subQ3}),makeQuery(id+"F11.opExtrude","SWEPT_EDGE",EDGE,{"disambiguationData":[OSD([subQ1,subQ0])]})]});}
            fillet(context, id + "F17", {"entities" : qUnion([Q0, Q1, Q2, Q3]), "radius" : 1 * mm, "tangentPropagation" : true, "allowEdgeOverflow" : false});
        }
        {
            var Q0;
            Q0=makeQuery(id+"F1.opExtrude","SWEPT_EDGE",EDGE,{"disambiguationData":[OSD([sQuery(id+"F0.wireOp",EDGE,"E0"),sQuery(id+"F0.wireOp",EDGE,"E3")])]});
            var Q1;
            Q1=makeQuery(id+"F1.opExtrude","SWEPT_EDGE",EDGE,{"disambiguationData":[OSD([sQuery(id+"F0.wireOp",EDGE,"E0"),sQuery(id+"F0.wireOp",EDGE,"E1")])]});
            var Q2;
            {var subQ0=sQuery(id+"F9.wireOp",EDGE,"E38");var subQ1=sQuery(id+"F9.wireOp",EDGE,"E37");var subQ7=sQuery(id+"F2.wireOp",EDGE,"E17.bottom");var subQ20=makeQuery(id+"F10.opExtrude","SWEPT_EDGE",EDGE,{"disambiguationData":[OSD([subQ1,subQ0])]});var subQ25=sQuery(id+"F2.wireOp",EDGE,"E17.top");Q2=makeQuery(id+"F11.boolean.opBoolean","MERGE",EDGE,{"derivedFrom":[makeQuery(id+"F10.boolean.opBoolean","COPY",EDGE,{"disambiguationData":[TD([makeQuery(id+"F3.boolean.opBoolean","COPY",FACE,{"derivedFrom":makeQuery(id+"F3.opExtrude","SWEPT_FACE",FACE,{"disambiguationData":[OSD([subQ25])]})})])],"derivedFrom":subQ20}),makeQuery(id+"F10.boolean.opBoolean","COPY",EDGE,{"disambiguationData":[TD([makeQuery(id+"F3.boolean.opBoolean","COPY",FACE,{"derivedFrom":makeQuery(id+"F3.opExtrude","SWEPT_FACE",FACE,{"disambiguationData":[OSD([subQ7])]})})])],"derivedFrom":subQ20}),makeQuery(id+"F11.opExtrude","SWEPT_EDGE",EDGE,{"disambiguationData":[OSD([subQ1,subQ0])]})]});}
            var Q3;
            {var subQ0=sQuery(id+"F9.wireOp",EDGE,"E37");var subQ1=sQuery(id+"F9.wireOp",EDGE,"E36");var subQ6=sQuery(id+"F2.wireOp",EDGE,"E17.bottom");var subQ20=makeQuery(id+"F10.opExtrude","SWEPT_EDGE",EDGE,{"disambiguationData":[OSD([subQ1,subQ0])]});var subQ25=sQuery(id+"F2.wireOp",EDGE,"E17.top");Q3=makeQuery(id+"F11.boolean.opBoolean","MERGE",EDGE,{"derivedFrom":[makeQuery(id+"F10.boolean.opBoolean","COPY",EDGE,{"disambiguationData":[TD([makeQuery(id+"F3.boolean.opBoolean","COPY",FACE,{"derivedFrom":makeQuery(id+"F3.opExtrude","SWEPT_FACE",FACE,{"disambiguationData":[OSD([subQ25])]})})])],"derivedFrom":subQ20}),makeQuery(id+"F10.boolean.opBoolean","COPY",EDGE,{"disambiguationData":[TD([makeQuery(id+"F3.boolean.opBoolean","COPY",FACE,{"derivedFrom":makeQuery(id+"F3.opExtrude","SWEPT_FACE",FACE,{"disambiguationData":[OSD([subQ6])]})})])],"derivedFrom":subQ20}),makeQuery(id+"F11.opExtrude","SWEPT_EDGE",EDGE,{"disambiguationData":[OSD([subQ1,subQ0])]})]});}
            var Q4;
            {var subQ0=sQuery(id+"F9.wireOp",EDGE,"E39");var subQ1=sQuery(id+"F9.wireOp",EDGE,"E36");var subQ2=sQuery(id+"F9.wireOp",EDGE,"E34");var subQ7=sQuery(id+"F2.wireOp",EDGE,"E17.bottom");var subQ21=makeQuery(id+"F10.opExtrude","SWEPT_EDGE",EDGE,{"disambiguationData":[OSD([subQ2,subQ1,subQ0])]});var subQ26=sQuery(id+"F2.wireOp",EDGE,"E17.top");Q4=makeQuery(id+"F12.boolean.opBoolean","MERGE",EDGE,{"derivedFrom":[makeQuery(id+"F10.boolean.opBoolean","COPY",EDGE,{"disambiguationData":[TD([makeQuery(id+"F3.boolean.opBoolean","COPY",FACE,{"derivedFrom":makeQuery(id+"F3.opExtrude","SWEPT_FACE",FACE,{"disambiguationData":[OSD([subQ26])]})})])],"derivedFrom":subQ21}),makeQuery(id+"F10.boolean.opBoolean","COPY",EDGE,{"disambiguationData":[TD([makeQuery(id+"F3.boolean.opBoolean","COPY",FACE,{"derivedFrom":makeQuery(id+"F3.opExtrude","SWEPT_FACE",FACE,{"disambiguationData":[OSD([subQ7])]})})])],"derivedFrom":subQ21}),makeQuery(id+"F11.opExtrude","SWEPT_EDGE",EDGE,{"disambiguationData":[OSD([subQ2,subQ1,subQ0])]}),makeQuery(id+"F12.opExtrude","SWEPT_EDGE",EDGE,{"disambiguationData":[OSD([subQ2,subQ1,subQ0])]})]});}
            fillet(context, id + "F18", {"entities" : qUnion([Q0, Q1, Q2, Q3, Q4]), "radius" : 0.6 * mm, "tangentPropagation" : true, "allowEdgeOverflow" : false});
        }
        {
            var Q0;
            Q0=makeQuery(id+"F1.opExtrude","SWEPT_FACE",FACE,{"disambiguationData":[OSD([sQuery(id+"F0.wireOp",EDGE,"E4")])]});
            var Q1;
            Q1=makeQuery(id+"F1.opExtrude","CAP_FACE",FACE,{"disambiguationData":[OSD([sQuery(id+"F0.wireOp",EDGE,"E0"),sQuery(id+"F0.wireOp",EDGE,"E1"),sQuery(id+"F0.wireOp",EDGE,"E3"),sQuery(id+"F0.wireOp",EDGE,"E4"),sQuery(id+"F0.wireOp",EDGE,"E6"),sQuery(id+"F0.wireOp",EDGE,"E8"),sQuery(id+"F0.wireOp",EDGE,"E9"),sQuery(id+"F0.wireOp",EDGE,"E10"),sQuery(id+"F0.wireOp",EDGE,"E11"),sQuery(id+"F0.wireOp",EDGE,"E12"),sQuery(id+"F0.wireOp",EDGE,"E13"),sQuery(id+"F0.wireOp",EDGE,"E14")])],"isStart":false});
            var Q2;
            Q2=makeQuery(id+"F1.opExtrude","CAP_FACE",FACE,{"disambiguationData":[OSD([sQuery(id+"F0.wireOp",EDGE,"E0"),sQuery(id+"F0.wireOp",EDGE,"E1"),sQuery(id+"F0.wireOp",EDGE,"E3"),sQuery(id+"F0.wireOp",EDGE,"E4"),sQuery(id+"F0.wireOp",EDGE,"E6"),sQuery(id+"F0.wireOp",EDGE,"E8"),sQuery(id+"F0.wireOp",EDGE,"E9"),sQuery(id+"F0.wireOp",EDGE,"E10"),sQuery(id+"F0.wireOp",EDGE,"E11"),sQuery(id+"F0.wireOp",EDGE,"E12"),sQuery(id+"F0.wireOp",EDGE,"E13"),sQuery(id+"F0.wireOp",EDGE,"E14")])],"isStart":true});
            var Q3;
            Q3=makeQuery(id+"F7.opExtrude","TWEAK_EDGE",EDGE,{"derivedFrom":[makeQuery(id+"F3.boolean.opBoolean","COPY",FACE,{"derivedFrom":makeQuery(id+"F3.opExtrude","SWEPT_FACE",FACE,{"disambiguationData":[OSD([sQuery(id+"F2.wireOp",EDGE,"E17.bottom")])]})}),makeQuery(id+"F6.imprint","IMPRINT",EDGE,{"derivedFrom":sQuery(id+"F6.wireOp",EDGE,"E27")})]});
            var Q4;
            Q4=makeQuery(id+"F3.boolean.opBoolean","INTERSECT",EDGE,{"derivedFrom":[makeQuery(id+"F1.opExtrude","SWEPT_FACE",FACE,{"disambiguationData":[OSD([sQuery(id+"F0.wireOp",EDGE,"E8")])]}),makeQuery(id+"F3.opExtrude","SWEPT_FACE",FACE,{"disambiguationData":[OSD([sQuery(id+"F2.wireOp",EDGE,"E17.bottom")])]})]});
            var Q5;
            Q5=makeQuery(id+"F5.opExtrude","TWEAK_EDGE",EDGE,{"derivedFrom":[makeQuery(id+"F3.boolean.opBoolean","COPY",FACE,{"derivedFrom":makeQuery(id+"F3.opExtrude","SWEPT_FACE",FACE,{"disambiguationData":[OSD([sQuery(id+"F2.wireOp",EDGE,"E17.top")])]})}),makeQuery(id+"F4.imprint","IMPRINT",EDGE,{"derivedFrom":sQuery(id+"F4.wireOp",EDGE,"E22")})]});
            var Q6;
            Q6=makeQuery(id+"F3.boolean.opBoolean","INTERSECT",EDGE,{"derivedFrom":[makeQuery(id+"F1.opExtrude","SWEPT_FACE",FACE,{"disambiguationData":[OSD([sQuery(id+"F0.wireOp",EDGE,"E8")])]}),makeQuery(id+"F3.opExtrude","SWEPT_FACE",FACE,{"disambiguationData":[OSD([sQuery(id+"F2.wireOp",EDGE,"E17.top")])]})]});
            fillet(context, id + "F19", {"entities" : qUnion([Q0, Q1, Q2, Q3, Q4, Q5, Q6]), "radius" : 0.2 * mm, "tangentPropagation" : true, "allowEdgeOverflow" : false});
        }
        {
            var Q0;
            Q0=makeQuery(id+"F1.opExtrude","SWEPT_EDGE",EDGE,{"disambiguationData":[OSD([sQuery(id+"F0.wireOp",EDGE,"E6"),sQuery(id+"F0.wireOp",EDGE,"E11")])]});
            var Q1;
            {var subQ0=sQuery(id+"F4.wireOp",EDGE,"E22");var subQ1=sQuery(id+"F0.wireOp",EDGE,"E8");var subQ3=sQuery(id+"F0.wireOp",EDGE,"E13");var subQ14=makeQuery(id+"F1.opExtrude","SWEPT_EDGE",EDGE,{"disambiguationData":[OSD([subQ1,subQ3])]});Q1=makeQuery(id+"F11.boolean.opBoolean","MERGE",EDGE,{"derivedFrom":[makeQuery(id+"F5.boolean.opBoolean","MERGE",EDGE,{"derivedFrom":[makeQuery(id+"F3.boolean.opBoolean","SPLIT",EDGE,{"disambiguationData":[TD([makeQuery(id+"F3.opExtrude","SWEPT_FACE",FACE,{"disambiguationData":[OSD([sQuery(id+"F2.wireOp",EDGE,"E17.top")])]})])],"derivedFrom":subQ14}),makeQuery(id+"F5.opExtrude","SWEPT_EDGE",EDGE,{"disambiguationData":[OSD([subQ1,subQ0,sQuery(id+"F4.wireOp",EDGE,"E25")])]})]}),makeQuery(id+"F7.boolean.opBoolean","MERGE",EDGE,{"derivedFrom":[makeQuery(id+"F3.boolean.opBoolean","SPLIT",EDGE,{"disambiguationData":[TD([makeQuery(id+"F3.opExtrude","SWEPT_FACE",FACE,{"disambiguationData":[OSD([sQuery(id+"F2.wireOp",EDGE,"E17.bottom")])]})])],"derivedFrom":subQ14}),makeQuery(id+"F7.opExtrude","SWEPT_EDGE",EDGE,{"disambiguationData":[OSD([subQ1,sQuery(id+"F6.wireOp",EDGE,"E27"),sQuery(id+"F6.wireOp",EDGE,"E30")])]})]}),makeQuery(id+"F11.opExtrude","SWEPT_EDGE",EDGE,{"disambiguationData":[OSD([subQ1,subQ0])]})]});}
            var Q2;
            {var subQ0=sQuery(id+"F4.wireOp",EDGE,"E22");var subQ1=sQuery(id+"F0.wireOp",EDGE,"E8");var subQ3=sQuery(id+"F0.wireOp",EDGE,"E13");var subQ14=makeQuery(id+"F1.opExtrude","SWEPT_EDGE",EDGE,{"disambiguationData":[OSD([subQ1,subQ3])]});Q2=makeQuery(id+"F11.boolean.opBoolean","MERGE",EDGE,{"derivedFrom":[makeQuery(id+"F5.boolean.opBoolean","MERGE",EDGE,{"derivedFrom":[makeQuery(id+"F3.boolean.opBoolean","SPLIT",EDGE,{"disambiguationData":[TD([makeQuery(id+"F3.opExtrude","SWEPT_FACE",FACE,{"disambiguationData":[OSD([sQuery(id+"F2.wireOp",EDGE,"E17.top")])]})])],"derivedFrom":subQ14}),makeQuery(id+"F5.opExtrude","SWEPT_EDGE",EDGE,{"disambiguationData":[OSD([subQ1,subQ0,sQuery(id+"F4.wireOp",EDGE,"E25")])]})]}),makeQuery(id+"F7.boolean.opBoolean","MERGE",EDGE,{"derivedFrom":[makeQuery(id+"F3.boolean.opBoolean","SPLIT",EDGE,{"disambiguationData":[TD([makeQuery(id+"F3.opExtrude","SWEPT_FACE",FACE,{"disambiguationData":[OSD([sQuery(id+"F2.wireOp",EDGE,"E17.bottom")])]})])],"derivedFrom":subQ14}),makeQuery(id+"F7.opExtrude","SWEPT_EDGE",EDGE,{"disambiguationData":[OSD([subQ1,sQuery(id+"F6.wireOp",EDGE,"E27"),sQuery(id+"F6.wireOp",EDGE,"E30")])]})]}),makeQuery(id+"F11.opExtrude","SWEPT_EDGE",EDGE,{"disambiguationData":[OSD([subQ1,subQ0])]})]});}
            var Q3;
            {var subQ0=sQuery(id+"F9.wireOp",EDGE,"E34");var subQ1=sQuery(id+"F4.wireOp",EDGE,"E22");var subQ2=makeQuery(id+"F10.opExtrude","SWEPT_FACE",FACE,{"disambiguationData":[OSD([subQ0])]});Q3=makeQuery(id+"F12.boolean.opBoolean","MERGE",EDGE,{"derivedFrom":[makeQuery(id+"F10.boolean.opBoolean","INTERSECT",EDGE,{"derivedFrom":[makeQuery(id+"F5.opExtrude","SWEPT_FACE",FACE,{"disambiguationData":[OSD([subQ1])]}),subQ2]}),makeQuery(id+"F10.boolean.opBoolean","INTERSECT",EDGE,{"derivedFrom":[makeQuery(id+"F7.opExtrude","SWEPT_FACE",FACE,{"disambiguationData":[OSD([sQuery(id+"F6.wireOp",EDGE,"E27")])]}),subQ2]}),makeQuery(id+"F12.opExtrude","SWEPT_EDGE",EDGE,{"disambiguationData":[OSD([subQ1,subQ0])]})]});}
            fillet(context, id + "F20", {"entities" : qUnion([Q0, Q1, Q2, Q3]), "radius" : 5 * mm, "tangentPropagation" : true, "allowEdgeOverflow" : false});
        }
    });
